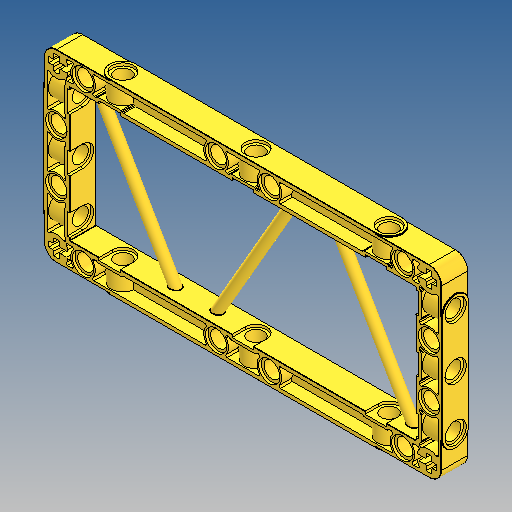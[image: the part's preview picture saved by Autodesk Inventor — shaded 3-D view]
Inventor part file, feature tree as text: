
AUTODESK INVENTOR PART (.ipt)
format: ipt  version: 2025 (Build 290162010, 162A)  size: 1,420,288 bytes
history: native  units: mm
features: sketch x12, extrude x9, projected_geometry x7, fillet x4, mirror x3, revolve x3, hole x2, delete_face x1
ambient origin geometry x8: Origin, YZ Plane, XZ Plane, XY Plane, X Axis, Y Axis, Z Axis, Center Point
bodies: Volumenkörper1 (feature_tree)
feature tree (41):
  extrude  "Extrusion1"  Depth=56.0mm
  fillet  "Rundung1"  Radius=24.0mm
  extrude  "Extrusion2"  Depth=4.0mm TaperAngle=0.0deg
  extrude  "Extrusion3"  Depth=8.0mm
  extrude  "Extrusion4"  Depth=40.0mm
  extrude  "Extrusion5"  Depth=1.6mm
  hole  "Bohrung1"  [1 undecoded]
  hole  "Bohrung2"  [1 undecoded]
  extrude  "Extrusion6"  Depth=5.6mm
  extrude  "Extrusion7"  Depth=3.6mm TaperAngle=0.0deg
  fillet  "Rundung2"  Radius=6.4mm
  fillet  "Rundung4"  Radius=0.8mm
  mirror  "Spiegeln1"
  extrude  "Extrusion8"  Depth=40.0mm
  extrude  "Extrusion9"  TaperAngle=45.0deg  [1 undecoded]
  mirror  "Spiegeln2"
  mirror  "Spiegeln3"
  sketch  "Skizze12"  dims[d32=3.6mm d33=0.4mm d34=7.2mm d35=8.0mm d36=2.8mm d37=16.0mm d38=7.2mm d39=10.0mm d40=0.0mm d41=4.8mm d42=6.0mm d43=6.4mm d44=0.5mm d45=90.0deg d46=8.0mm d47=20.594885mm d48=4.8mm d49=6.0mm d50=6.4mm d51=0.5mm d52=90.0deg d53=8.0mm d54=20.594885mm d55=0.3mm d56=0.0mm d57=0.3mm d58=0.0mm d59=4.0mm d60=4.0mm d61=0.1mm d62=0.8mm d63=0.0mm d64=0.8mm d65=0.0mm d66=60.0deg d67=60.0deg d68=12.701706mm d69=62.0mm d70=12.701706mm d71=1.5mm d72=90.0deg d73=90.0deg d74=90.0deg d75=0.1mm d76=0.4mm]
  revolve  "Umdrehung1"
  revolve  "Umdrehung2"
  revolve  "Umdrehung3"
  delete_face  "Fläche löschen1"
  fillet  "Rundung3"  Radius=0.4mm
  sketch  "Skizze1"  dims[d0=3.7mm d1=56.0mm d2=24.0mm]
  sketch  "Skizze2"  dims[d3=0.1mm d6=4.0mm d7=0.0mm]
  sketch  "Skizze3"  dims[d8=8.0mm d9=8.0mm]
  sketch  "Skizze4"  dims[d10=4.8mm d11=40.0mm]
  sketch  "Skizze5"  dims[d12=1.6mm d13=1.6mm]
  sketch  "Skizze6"  dims[d14=3.7mm d15=5.6mm]
  projected_geometry  "Projizierte Kontur1"
  sketch  "Skizze7"  dims[d16=0.4mm d17=0.4mm]
  sketch  "Skizze8"  dims[d18=0.4mm d19=5.6mm]
  sketch  "Skizze9"  dims[d20=0.4mm d21=3.6mm d22=0.0mm d23=6.4mm d24=0.8mm d25=0.0mm]
  sketch  "Skizze10"  dims[d26=7.2mm d27=40.0mm]
  sketch  "Skizze11"  dims[d28=0.8mm d29=0.0mm d30=45.0deg d31=0.4mm]
  projected_geometry  "Projizierte Kontur2"
  projected_geometry  "Projizierte Kontur3"
  projected_geometry  "Projizierte Kontur4"
  projected_geometry  "Projizierte Kontur5"
  projected_geometry  "Projizierte Kontur6"
  projected_geometry  "Projizierte Kontur7"
note: 3 required parameter values undecoded (feature->parameter linkage not recoverable at this tier; creation-order binding heuristic only, values carry confidence <= 0.55)
